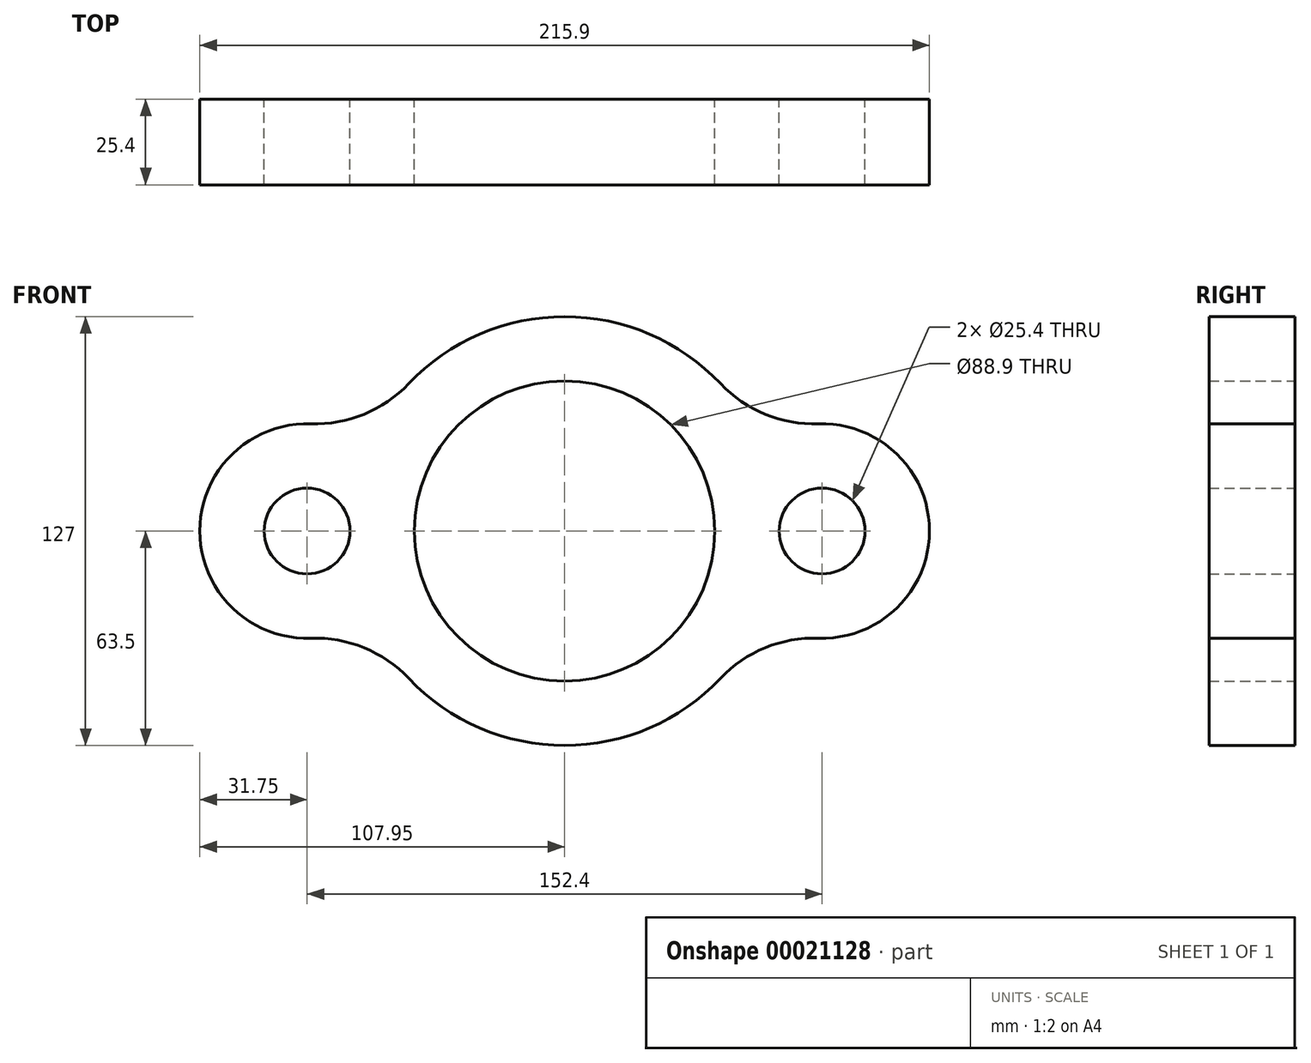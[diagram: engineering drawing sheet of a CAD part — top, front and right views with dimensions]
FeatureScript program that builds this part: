
annotation { "Feature Type Name" : "Feature", "Feature Type Description" : "" }
export const myFeature = defineFeature(function(context is Context, id is Id, definition is map)
    precondition{}
    {
        {
            var Q0;
            Q0=qCreatedBy(makeId("Front.planeOp"),FACE);
            var sketch = newSketch(context, id + "F0", { "sketchPlane" : qUnion([Q0])});
            skCircle(sketch, "E0", {"center": v(0, 0) * mm, "radius": 63.5 * mm});
            skCircle(sketch, "E1", {"center": v(-76.2, 0) * mm, "radius": 31.75 * mm});
            skArc(sketch, "E2", {"start": v(-75.12, 31.73) * mm, "mid": v(-59.35, 34.56) * mm, "end": v(-46.14, 43.63) * mm});
            skArc(sketch, "E3", {"start": v(-46.14, -43.63) * mm, "mid": v(-59.35, -34.56) * mm, "end": v(-75.12, -31.73) * mm});
            skCircle(sketch, "E4", {"center": v(-76.2, 0) * mm, "radius": 12.7 * mm});
            skCircle(sketch, "E5", {"center": v(76.2, 0) * mm, "radius": 12.7 * mm});
            skCircle(sketch, "E6", {"center": v(76.2, 0) * mm, "radius": 31.75 * mm});
            skArc(sketch, "E7", {"start": v(46.14, 43.63) * mm, "mid": v(59.35, 34.56) * mm, "end": v(75.12, 31.73) * mm});
            skArc(sketch, "E8", {"start": v(75.12, -31.73) * mm, "mid": v(59.35, -34.56) * mm, "end": v(46.14, -43.63) * mm});
            skCircle(sketch, "E9", {"center": v(0, 0) * mm, "radius": 44.45 * mm});
            skSolve(sketch);
        }
        {
            var Q0;
            Q0 = qSketchRegion(id + "F0", true);
            var Q1;
            {var subQ1=sQuery(id+"F0.wireOp",EDGE,"E1");var subQ5=makeQuery(id+"F0.imprint","INTERSECT",VERTEX,{"derivedFrom":[sQuery(id+"F0.wireOp",EDGE,"E0"),subQ1]});Q1=makeQuery(id+"F0.imprint","IMPRINT",FACE,{"disambiguationData":[TD([[makeQuery(id+"F0.imprint","IMPRINT",EDGE,{"disambiguationData":[TD([[subQ5,-1.0]])],"derivedFrom":subQ1}),1.0]])]});}
            var Q2;
            {var subQ1=sQuery(id+"F0.wireOp",EDGE,"be363ea8-68e0-4b47-8c0d-d1a181a57841");var subQ5=makeQuery(id+"F0.imprint","INTERSECT",VERTEX,{"derivedFrom":[sQuery(id+"F0.wireOp",EDGE,"E0"),subQ1]});Q2=makeQuery(id+"F0.imprint","IMPRINT",FACE,{"disambiguationData":[TD([[makeQuery(id+"F0.imprint","IMPRINT",EDGE,{"disambiguationData":[TD([[subQ5,1.0]])],"derivedFrom":subQ1}),1.0]])]});}
            var Q3;
            {var subQ3=sQuery(id+"F0.wireOp",EDGE,"d5fdc14e-b83c-4a82-9787-2c73df4196e7");var subQ5=sQuery(id+"F0.wireOp",EDGE,"E0");var subQ6=makeQuery(id+"F0.imprint","INTERSECT",VERTEX,{"derivedFrom":[subQ5,subQ3]});Q3=makeQuery(id+"F0.imprint","IMPRINT",FACE,{"disambiguationData":[TD([[makeQuery(id+"F0.imprint","IMPRINT",EDGE,{"disambiguationData":[TD([[subQ6,-1.0]])],"derivedFrom":subQ5}),-1.0]])]});}
            var Q4;
            {var subQ2=sQuery(id+"F0.wireOp",EDGE,"E0");var subQ5=makeQuery(id+"F0.imprint","INTERSECT",VERTEX,{"derivedFrom":[subQ2,sQuery(id+"F0.wireOp",EDGE,"E5")]});Q4=makeQuery(id+"F0.imprint","IMPRINT",FACE,{"disambiguationData":[TD([[makeQuery(id+"F0.imprint","IMPRINT",EDGE,{"disambiguationData":[TD([[subQ5,-1.0]])],"derivedFrom":subQ2}),1.0]])]});}
            extrude(context, id + "F1", {"entities" : qUnion([Q0, Q1, Q2, Q3, Q4]), "depth" : 25.4 * mm});
        }
    });
